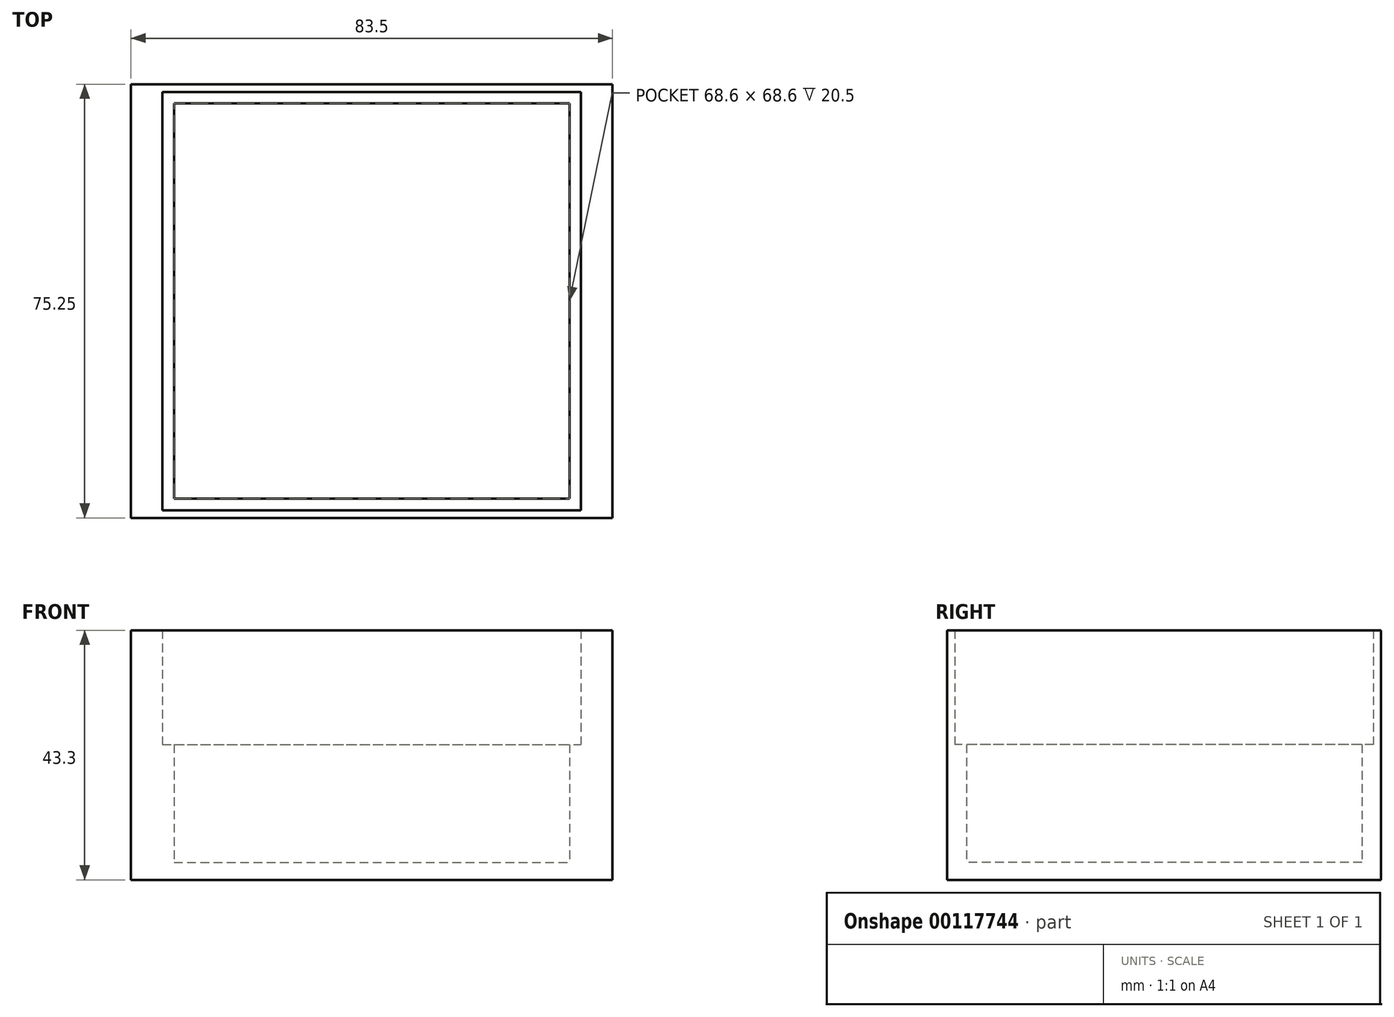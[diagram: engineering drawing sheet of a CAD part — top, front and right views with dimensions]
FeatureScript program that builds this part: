
annotation { "Feature Type Name" : "Feature", "Feature Type Description" : "" }
export const myFeature = defineFeature(function(context is Context, id is Id, definition is map)
    precondition{}
    {
        {
            var Q0;
            Q0=qCreatedBy(makeId("Top.planeOp"),FACE);
            var sketch = newSketch(context, id + "F0", { "sketchPlane" : qUnion([Q0])});
            skLineSegment(sketch, "E0.bottom", {"start": v(0, 0) * mm, "end": v(68.6, 0) * mm});
            skLineSegment(sketch, "E0.top", {"start": v(0, -68.6) * mm, "end": v(68.6, -68.6) * mm});
            skLineSegment(sketch, "E0.left", {"start": v(0, 0) * mm, "end": v(0, -68.6) * mm});
            skLineSegment(sketch, "E0.right", {"start": v(68.6, 0) * mm, "end": v(68.6, -68.6) * mm});
            skLineSegment(sketch, "E1.bottom", {"start": v(-2, 2) * mm, "end": v(70.6, 2) * mm});
            skLineSegment(sketch, "E1.top", {"start": v(-2, -70.6) * mm, "end": v(70.6, -70.6) * mm});
            skLineSegment(sketch, "E1.left", {"start": v(-2, 2) * mm, "end": v(-2, -70.6) * mm});
            skLineSegment(sketch, "E1.right", {"start": v(70.6, 2) * mm, "end": v(70.6, -70.6) * mm});
            skLineSegment(sketch, "E2.bottom", {"start": v(-7.45, 3.33) * mm, "end": v(76.05, 3.33) * mm});
            skLineSegment(sketch, "E2.top", {"start": v(-7.45, -71.92) * mm, "end": v(76.05, -71.92) * mm});
            skLineSegment(sketch, "E2.left", {"start": v(-7.45, 3.32) * mm, "end": v(-7.45, -71.92) * mm});
            skLineSegment(sketch, "E2.right", {"start": v(76.05, 3.32) * mm, "end": v(76.05, -71.92) * mm});
            skLineSegment(sketch, "E3.bottom", {"start": v(-9.45, 5.32) * mm, "end": v(78.05, 5.32) * mm});
            skLineSegment(sketch, "E3.top", {"start": v(-9.45, -73.92) * mm, "end": v(78.05, -73.92) * mm});
            skLineSegment(sketch, "E3.left", {"start": v(-9.45, 5.32) * mm, "end": v(-9.45, -73.92) * mm});
            skLineSegment(sketch, "E3.right", {"start": v(78.05, 5.32) * mm, "end": v(78.05, -73.92) * mm});
            skLineSegment(sketch, "E4.bottom", {"start": v(-13.68, 13.68) * mm, "end": v(82.28, 13.68) * mm});
            skLineSegment(sketch, "E4.top", {"start": v(-13.68, -82.28) * mm, "end": v(82.28, -82.28) * mm});
            skLineSegment(sketch, "E4.left", {"start": v(-13.68, 13.68) * mm, "end": v(-13.68, -82.28) * mm});
            skLineSegment(sketch, "E4.right", {"start": v(82.28, 13.68) * mm, "end": v(82.28, -82.28) * mm});
            skPoint(sketch, "E5", {"position": v(34.3, 0) * mm});
            skPoint(sketch, "E6", {"position": v(34.3, 2) * mm});
            skPoint(sketch, "E7", {"position": v(0, -34.3) * mm});
            skPoint(sketch, "E8", {"position": v(-2, -34.3) * mm});
            skPoint(sketch, "E9", {"position": v(-7.45, -34.3) * mm});
            skPoint(sketch, "E10", {"position": v(34.3, 3.33) * mm});
            skPoint(sketch, "E11", {"position": v(34.3, 13.68) * mm});
            skPoint(sketch, "E12", {"position": v(-13.68, -34.3) * mm});
            skLineSegment(sketch, "E13.bottom", {"start": v(-15.68, 15.68) * mm, "end": v(84.28, 15.68) * mm});
            skLineSegment(sketch, "E13.top", {"start": v(-15.68, -84.28) * mm, "end": v(84.28, -84.28) * mm});
            skLineSegment(sketch, "E13.left", {"start": v(-15.68, 15.68) * mm, "end": v(-15.68, -84.28) * mm});
            skLineSegment(sketch, "E13.right", {"start": v(84.28, 15.68) * mm, "end": v(84.28, -84.28) * mm});
            skSolve(sketch);
        }
        {
            var Q0;
            Q0=makeQuery(id+"F0.imprint","IMPRINT",FACE,{"disambiguationData":[TD([[makeQuery(id+"F0.imprint","IMPRINT",EDGE,{"derivedFrom":sQuery(id+"F0.wireOp",EDGE,"E0.bottom")}),-1.0]])]});
            extrude(context, id + "F1", {"entities" : qUnion([Q0]), "depth" : 3 * mm});
        }
        {
            var Q0;
            Q0=makeQuery(id+"F0.imprint","IMPRINT",FACE,{"disambiguationData":[TD([[makeQuery(id+"F0.imprint","IMPRINT",EDGE,{"derivedFrom":sQuery(id+"F0.wireOp",EDGE,"E0.bottom")}),1.0]])]});
            extrude(context, id + "F2", {"entities" : qUnion([Q0]), "operationType" : NewBodyOperationType.ADD, "depth" : 23.5 * mm});
        }
        {
            var Q0;
            Q0=makeQuery(id+"F0.imprint","IMPRINT",FACE,{"disambiguationData":[TD([[makeQuery(id+"F0.imprint","IMPRINT",EDGE,{"derivedFrom":sQuery(id+"F0.wireOp",EDGE,"E1.bottom")}),1.0]])]});
            extrude(context, id + "F3", {"entities" : qUnion([Q0]), "operationType" : NewBodyOperationType.ADD, "depth" : 43.3 * mm});
        }
    });
